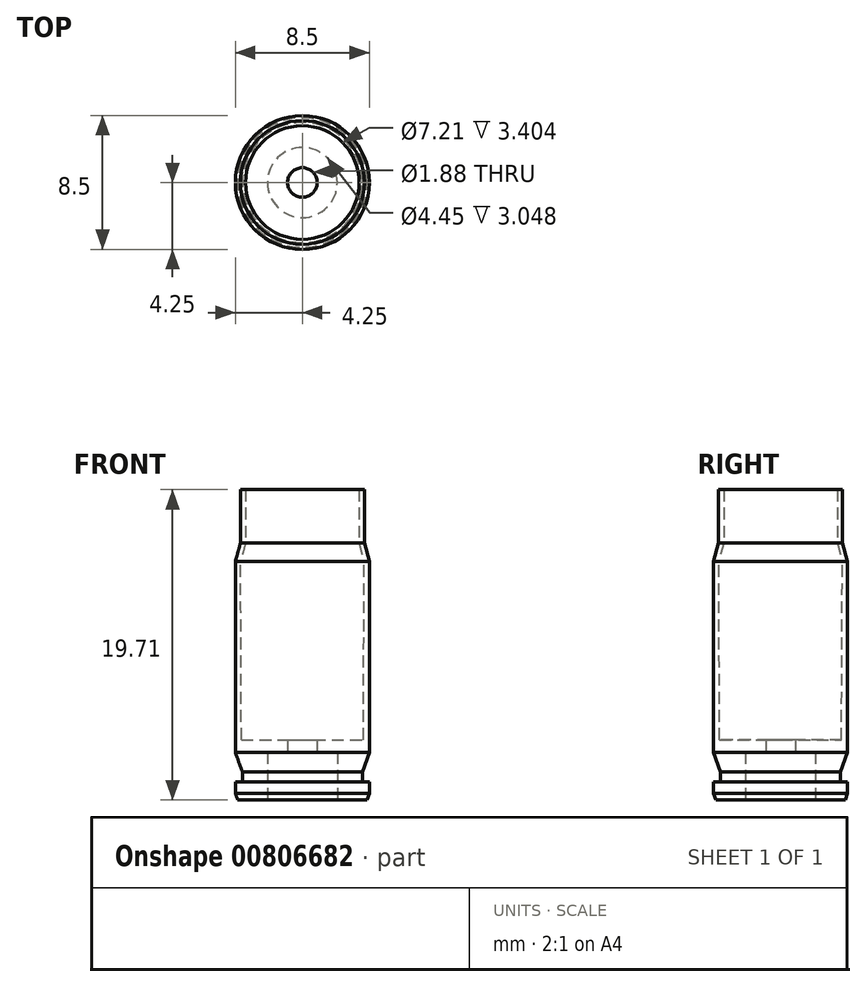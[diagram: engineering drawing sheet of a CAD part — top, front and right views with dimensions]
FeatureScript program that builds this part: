
annotation { "Feature Type Name" : "Feature", "Feature Type Description" : "" }
export const myFeature = defineFeature(function(context is Context, id is Id, definition is map)
    precondition{}
    {
        {
            var Q0;
            Q0=qCreatedBy(makeId("Front.planeOp"),FACE);
            var sketch = newSketch(context, id + "F0", { "sketchPlane" : qUnion([Q0])});
            skLineSegment(sketch, "E0", {"start": v(2.22, 0) * mm, "end": v(4.1, 0) * mm});
            skLineSegment(sketch, "E1", {"start": v(4.25, 0.4) * mm, "end": v(4.25, 1.14) * mm});
            skLineSegment(sketch, "E2", {"start": v(4.25, 1.14) * mm, "end": v(3.81, 1.14) * mm});
            skLineSegment(sketch, "E3", {"start": v(4.25, 3) * mm, "end": v(4.25, 15.14) * mm});
            skLineSegment(sketch, "E4", {"start": v(4.25, 15.14) * mm, "end": v(3.94, 16.3) * mm});
            skLineSegment(sketch, "E5", {"start": v(3.94, 16.3) * mm, "end": v(3.94, 19.71) * mm});
            skLineSegment(sketch, "E6", {"start": v(3.94, 19.71) * mm, "end": v(3.6, 19.71) * mm});
            skLineSegment(sketch, "E7", {"start": v(3.6, 19.71) * mm, "end": v(3.6, 16.3) * mm});
            skLineSegment(sketch, "E8", {"start": v(3.6, 16.3) * mm, "end": v(3.92, 15.14) * mm});
            skLineSegment(sketch, "E9", {"start": v(3.92, 15.14) * mm, "end": v(3.87, 3.8) * mm});
            skLineSegment(sketch, "E10", {"start": v(0.94, 3.81) * mm, "end": v(0.94, 3.05) * mm});
            skLineSegment(sketch, "E11", {"start": v(0.94, 3.05) * mm, "end": v(2.22, 3.05) * mm});
            skLineSegment(sketch, "E12", {"start": v(2.22, 3.05) * mm, "end": v(2.22, 0) * mm});
            skLineSegment(sketch, "E13", {"start": v(3.81, 1.14) * mm, "end": v(3.81, 1.78) * mm});
            skLineSegment(sketch, "E14", {"start": v(3.81, 1.78) * mm, "end": v(4.25, 3) * mm});
            skLineSegment(sketch, "E15", {"start": v(0.94, 3.81) * mm, "end": v(3.87, 3.8) * mm});
            skPoint(sketch, "E16.orphan", {"position": v(3.87, 3) * mm});
            skLineSegment(sketch, "E17", {"start": v(4.25, 0.4) * mm, "end": v(4.1, 0) * mm});
            skPoint(sketch, "E18.orphan", {"position": v(4.25, 0) * mm});
            skLineSegment(sketch, "E19", {"start": v(0, 0) * mm, "end": v(0, 23) * mm});
            skSolve(sketch);
        }
        {
            var Q0;
            Q0 = qSketchRegion(id + "F0", true);
            var Q1;
            Q1=sQuery(id+"F0.wireOp",EDGE,"E19");
            revolve(context, id + "F1", {"surfaceOperationType" : NewSurfaceOperationType.NEW, "entities" : qUnion([Q0]), "axis" : qUnion([Q1]), "revolveType" : RevolveType.FULL});
        }
        {
            var Q0;
            Q0=makeQuery(id+"F1.opRevolve","SWEPT_BODY",BODY,{"disambiguationData":[OSD([sQuery(id+"F0.wireOp",EDGE,"E0"),sQuery(id+"F0.wireOp",EDGE,"E1"),sQuery(id+"F0.wireOp",EDGE,"E2"),sQuery(id+"F0.wireOp",EDGE,"E3"),sQuery(id+"F0.wireOp",EDGE,"E4"),sQuery(id+"F0.wireOp",EDGE,"E5"),sQuery(id+"F0.wireOp",EDGE,"E6"),sQuery(id+"F0.wireOp",EDGE,"E7"),sQuery(id+"F0.wireOp",EDGE,"E8"),sQuery(id+"F0.wireOp",EDGE,"E9"),sQuery(id+"F0.wireOp",EDGE,"E10"),sQuery(id+"F0.wireOp",EDGE,"E11"),sQuery(id+"F0.wireOp",EDGE,"E12"),sQuery(id+"F0.wireOp",EDGE,"E13"),sQuery(id+"F0.wireOp",EDGE,"E14"),sQuery(id+"F0.wireOp",EDGE,"E15"),sQuery(id+"F0.wireOp",EDGE,"E17")])]});
            transform(context, id + "F2", {"entities" : qUnion([Q0]), "transformType" : TransformType.TRANSLATION_3D, "dx" : 0 * mm, "dy" : 0 * mm, "dz" : 0 * mm, "makeCopy" : true});
        }
        {
            var Q0;
            Q0=makeQuery(id+"F2.opPattern","COPY",BODY,{"derivedFrom":makeQuery(id+"F1.opRevolve","SWEPT_BODY",BODY,{"disambiguationData":[OSD([sQuery(id+"F0.wireOp",EDGE,"E0"),sQuery(id+"F0.wireOp",EDGE,"E1"),sQuery(id+"F0.wireOp",EDGE,"E2"),sQuery(id+"F0.wireOp",EDGE,"E3"),sQuery(id+"F0.wireOp",EDGE,"E4"),sQuery(id+"F0.wireOp",EDGE,"E5"),sQuery(id+"F0.wireOp",EDGE,"E6"),sQuery(id+"F0.wireOp",EDGE,"E7"),sQuery(id+"F0.wireOp",EDGE,"E8"),sQuery(id+"F0.wireOp",EDGE,"E9"),sQuery(id+"F0.wireOp",EDGE,"E10"),sQuery(id+"F0.wireOp",EDGE,"E11"),sQuery(id+"F0.wireOp",EDGE,"E12"),sQuery(id+"F0.wireOp",EDGE,"E13"),sQuery(id+"F0.wireOp",EDGE,"E14"),sQuery(id+"F0.wireOp",EDGE,"E15"),sQuery(id+"F0.wireOp",EDGE,"E17")])]}),"instanceName":"1"});
            deleteBodies(context, id + "F3", {"entities" : qUnion([Q0])});
        }
    });
